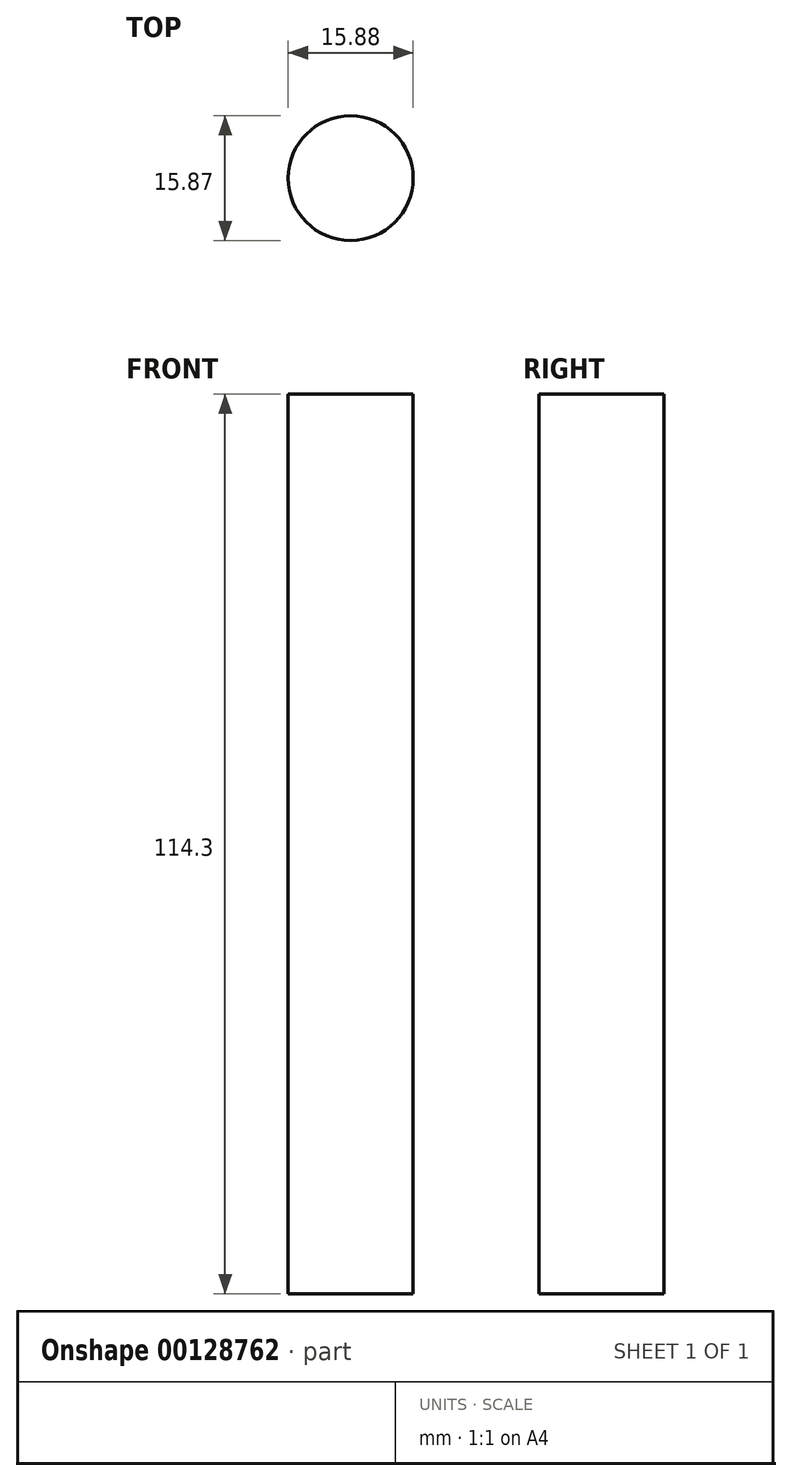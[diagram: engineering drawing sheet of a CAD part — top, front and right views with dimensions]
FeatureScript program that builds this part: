
annotation { "Feature Type Name" : "Feature", "Feature Type Description" : "" }
export const myFeature = defineFeature(function(context is Context, id is Id, definition is map)
    precondition{}
    {
        {
            var Q0;
            Q0=qCreatedBy(makeId("Top.planeOp"),FACE);
            var sketch = newSketch(context, id + "F0", { "sketchPlane" : qUnion([Q0])});
            skCircle(sketch, "E0", {"center": v(0, 0.61) * mm, "radius": 7.94 * mm});
            skSolve(sketch);
        }
        {
            var Q0;
            Q0=makeQuery(id+"F0.imprint","IMPRINT",FACE,{"disambiguationData":[TD([[makeQuery(id+"F0.imprint","IMPRINT",EDGE,{"derivedFrom":sQuery(id+"F0.wireOp",EDGE,"E0")}),1.0]])]});
            extrude(context, id + "F1", {"entities" : qUnion([Q0]), "depth" : 114.3 * mm});
        }
    });
